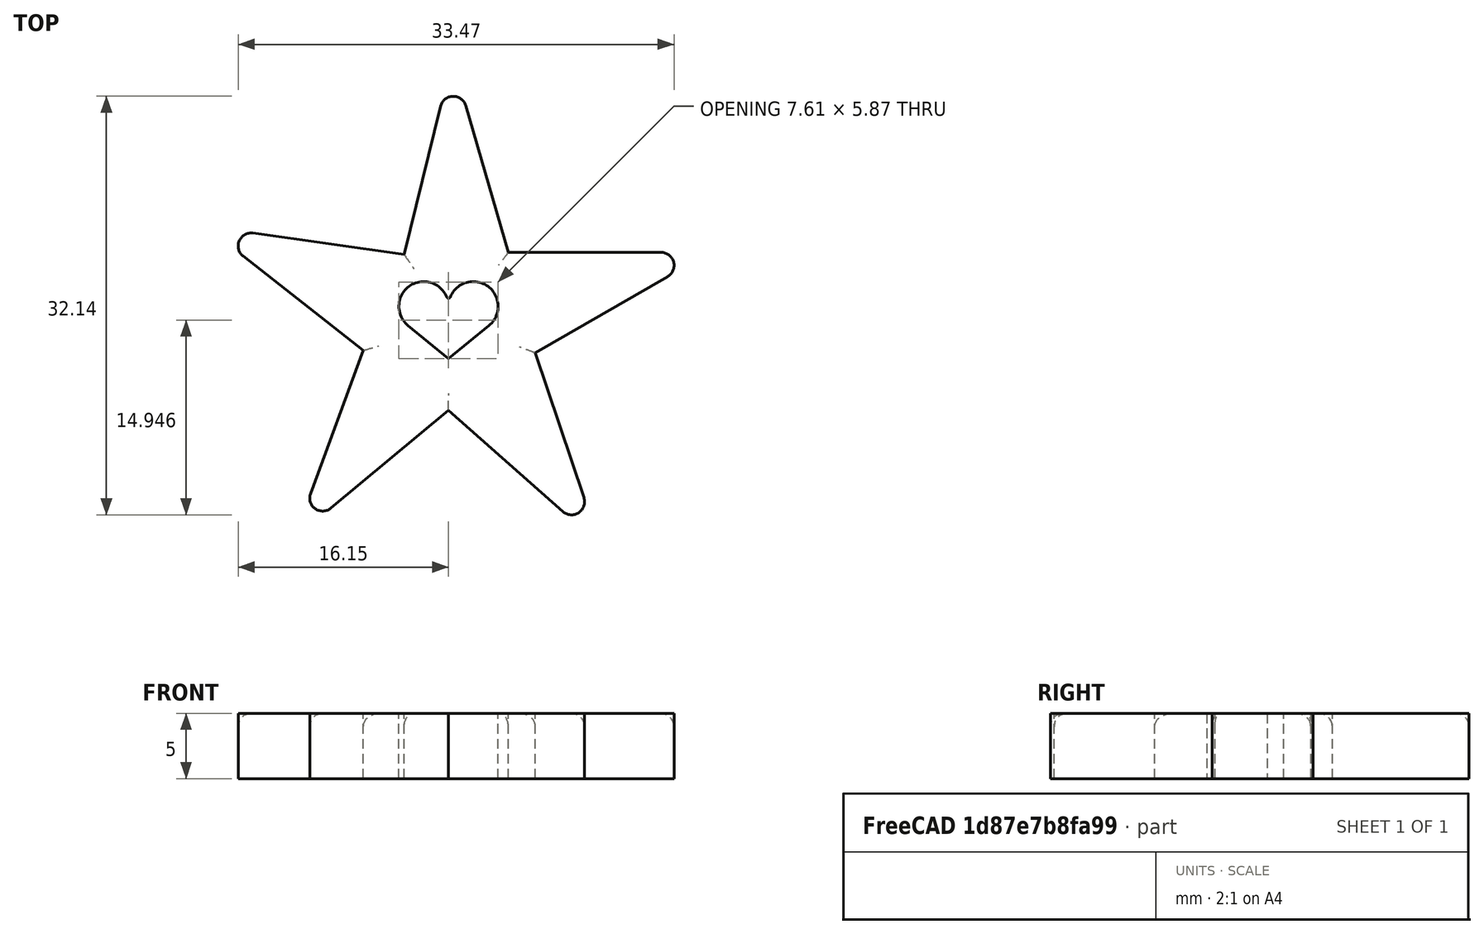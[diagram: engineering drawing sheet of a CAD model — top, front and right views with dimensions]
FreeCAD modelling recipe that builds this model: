
FCSTD DOCUMENT  (FreeCAD 0.16R)
Label: heartstar
License: All rights reserved
LicenseURL: http://en.wikipedia.org/wiki/All_rights_reserved
objects: PartDesign::Fillet×4, Sketcher::SketchObject×2, PartDesign::Pad×1, PartDesign::Pocket×1, Mesh::Feature×1
note: 10 computed .brp shape members not serialized (recipe doc carries the construction recipe); baked Part::Feature solids carry a one-line shape summary decoded from their .brp

FEATURE [Sketcher::SketchObject] Sketch
  sketch-geometry (10):
    g0: LineSegment StartX=-3.40063 StartY=17.9826 StartZ=0 EndX=0.291263 EndY=32.9899 EndZ=0
    g1: LineSegment StartX=0.291263 StartY=32.9899 StartZ=0 EndX=4.59768 EndY=18.1472 EndZ=0
    g2: LineSegment StartX=4.59768 StartY=18.1472 StartZ=0 EndX=20.0525 EndY=18.1472 EndZ=0
    g3: LineSegment StartX=20.0525 StartY=18.1472 StartZ=0 EndX=6.66823 EndY=10.4198 EndZ=0
    g4: LineSegment StartX=6.66823 StartY=10.4198 StartZ=0 EndX=11.5816 EndY=-4.23318 EndZ=0
    g5: LineSegment StartX=11.5816 StartY=-4.23318 StartZ=0 EndX=0 EndY=6 EndZ=0
    g6: LineSegment StartX=0 StartY=6 StartZ=0 EndX=-11.8872 EndY=-3.87656 EndZ=0
    g7: LineSegment StartX=-11.8872 StartY=-3.87656 StartZ=0 EndX=-6.53086 EndY=10.6204 EndZ=0
    g8: LineSegment StartX=-6.53086 StartY=10.6204 StartZ=0 EndX=-18.7038 EndY=20.1426 EndZ=0
    g9: LineSegment StartX=-18.7038 StartY=20.1426 StartZ=0 EndX=-3.40063 EndY=17.9826 EndZ=0
  constraints (30):
    c: Coincident(g0,g1)
    c: Coincident(g1,g2)
    c: Horizontal(g2)
    c: Coincident(g2,g3)
    c: Coincident(g3,g4)
    c: Coincident(g4,g5)
    c: PointOnObject(g5,g-2)
    c: Coincident(g5,g6)
    c: Coincident(g6,g7)
    c: Coincident(g7,g8)
    c: Coincident(g8,g9)
    c: Coincident(g0,g9)
    c: Angle(g0,g1) = 0.523599
    c: Angle(g2,g3) = 0.523599
    c: Angle(g4,g5) = 0.523599
    c: Angle(g6,g7) = 0.523599
    c: Angle(g8,g9) = 0.523599
    c: Equal(g0,g1)
    c: Equal(g1,g2)
    c: Equal(g2,g3)
    c: Equal(g3,g4)
    c: Equal(g4,g5)
    c: Equal(g5,g6)
    c: Equal(g6,g7)
    c: Equal(g7,g8)
    c: Equal(g8,g9)
    c: DistanceY(g-1,g5) = 6
    c: Distance(g3,g5) = 8
    c: DistanceY(g4) = -4.23318
    c: DistanceY(g4,g6) = 0.356622
FEATURE [PartDesign::Pad] Pad
  Length = 5
  Length2 = 100
  Sketch = -> Sketch
  Type = 0
FEATURE [PartDesign::Fillet] Fillet
  Base = -> Pad [Edge8]
  Radius = 1
FEATURE [PartDesign::Fillet] Fillet001
  Base = -> Fillet [Edge30,Edge33,Edge29,Edge17]
  Radius = 1
FEATURE [Sketcher::SketchObject] Sketch001
  Placement = pos=(0,0,5) rot=(0,0,1;0rad)
  Support = -> Fillet001 [Face17]
  sketch-geometry (4):
    g0: ArcOfCircle CenterX=1.90344 CenterY=14 CenterZ=0 NormalX=0 NormalY=0 NormalZ=1 Radius=1.90344 StartAngle=5.39489 EndAngle=9.42478
    g1: ArcOfCircle CenterX=-1.90344 CenterY=14 CenterZ=0 NormalX=0 NormalY=0 NormalZ=1 Radius=1.90344 StartAngle=0 EndAngle=4.02989
    g2: LineSegment StartX=3.10401 StartY=12.5229 StartZ=0 EndX=0 EndY=10 EndZ=0
    g3: LineSegment StartX=0 StartY=10 StartZ=0 EndX=-3.10401 EndY=12.5229 EndZ=0
  constraints (13):
    c: PointOnObject(g0,g-2)
    c: PointOnObject(g2,g-2)
    c: Coincident(g2,g3)
    c: Coincident(g2,g0)
    c: Tangent(g0,g2)
    c: Coincident(g3,g1)
    c: Tangent(g3,g1)
    c: Coincident(g0,g1)
    c: Symmetric(g0,g1,g0)
    c: DistanceY(g0) = 14
    c: DistanceY(g1) = 14
    c: DistanceY(g2) = 10
    c: DistanceX(g1) = -3.10401
FEATURE [PartDesign::Pocket] Pocket
  Length = 5
  Sketch = -> Sketch001
  Type = 0
FEATURE [PartDesign::Fillet] Fillet002
  Base = -> Pocket [Edge55]
  Radius = 0.15
FEATURE [PartDesign::Fillet] Fillet003
  Base = -> Fillet002 [Edge49,Edge45,Edge37,Edge33,Edge39,Edge43,Edge51,Edge55,Edge60,Edge57]
  Radius = 1
FEATURE [Mesh::Feature] Mesh  label="Fillet003 (Meshed)"
